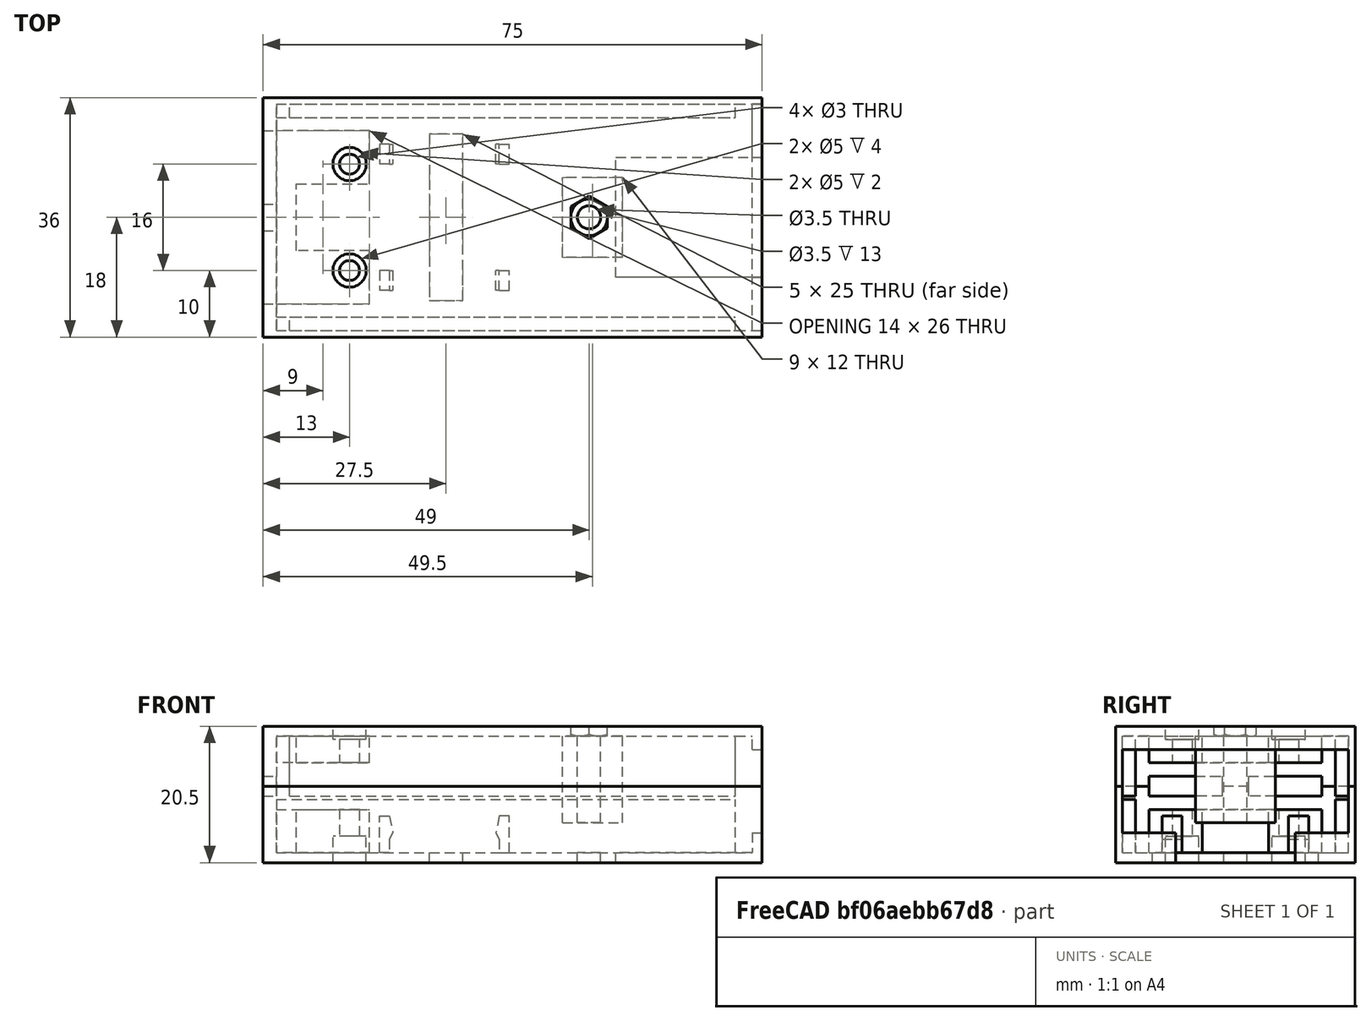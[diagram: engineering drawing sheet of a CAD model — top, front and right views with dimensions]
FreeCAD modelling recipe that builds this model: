
FCSTD DOCUMENT  (FreeCAD 0.17R13522 (Git))
Label: CubeSensor
License: All rights reserved
LicenseURL: http://en.wikipedia.org/wiki/All_rights_reserved
objects: Part::Box×13, Part::Extrusion×9, Sketcher::SketchObject×7, Part::MultiFuse×6, Part::Cylinder×6, Mesh::Feature×3, Part::Cut×2
note: 43 computed .brp shape members not serialized (recipe doc carries the construction recipe); baked Part::Feature solids carry a one-line shape summary decoded from their .brp

FEATURE [Mesh::Feature] dht22
  Placement = pos=(31,0,3) rot=(-0.707107,-0.707107,0;3.14159rad)
FEATURE [Mesh::Feature] gy_30  label="gy-30"
  Placement = pos=(48,16,3) rot=(-0.57735,0.57735,0.57735;4.18879rad)
FEATURE [Mesh::Feature] moisture_sensor
  Placement = pos=(-46,0,10) rot=(0,0,1;0rad)
FEATURE [Sketcher::SketchObject] Sketch
  MapMode = 5
  sketch-geometry (12):
    g0: LineSegment StartX=-25 StartY=18 StartZ=0 EndX=-25 EndY=-18 EndZ=0
    g1: LineSegment StartX=-25 StartY=-18 StartZ=0 EndX=50 EndY=-18 EndZ=0
    g2: LineSegment StartX=50 StartY=-18 StartZ=0 EndX=50 EndY=-9 EndZ=0
    g3: LineSegment StartX=50 StartY=-9 StartZ=0 EndX=28 EndY=-9 EndZ=0
    g4: LineSegment StartX=28 StartY=-9 StartZ=0 EndX=28 EndY=9 EndZ=0
    g5: LineSegment StartX=28 StartY=9 StartZ=0 EndX=50 EndY=9 EndZ=0
    g6: LineSegment StartX=50 StartY=9 StartZ=0 EndX=50 EndY=18 EndZ=0
    g7: LineSegment StartX=50 StartY=18 StartZ=0 EndX=-25 EndY=18 EndZ=0
    g8: LineSegment StartX=3e-12 StartY=-12.5 StartZ=0 EndX=5 EndY=-12.5 EndZ=0
    g9: LineSegment StartX=5 StartY=-12.5 StartZ=0 EndX=5 EndY=12.5 EndZ=0
    g10: LineSegment StartX=5 StartY=12.5 StartZ=0 EndX=-3e-12 EndY=12.5 EndZ=0
    g11: LineSegment StartX=-3e-12 StartY=12.5 StartZ=0 EndX=3e-12 EndY=-12.5 EndZ=0
  constraints (35):
    c: Coincident(g0,g1)
    c: Coincident(g0,g7)
    c: Coincident(g11,g10)
    c: Coincident(g9,g10)
    c: Coincident(g11,g8)
    c: Coincident(g9,g8)
    c: Coincident(g7,g6)
    c: Coincident(g6,g5)
    c: Coincident(g5,g4)
    c: Coincident(g4,g3)
    c: Coincident(g2,g3)
    c: Coincident(g1,g2)
    c: Parallel(g8,g1)
    c: Parallel(g1,g3)
    c: Parallel(g3,g5)
    c: Parallel(g5,g10)
    c: Parallel(g10,g7)
    c: Parallel(g7,g-1)
    c: Parallel(g0,g11)
    c: Parallel(g11,g9)
    c: Parallel(g9,g4)
    c: Parallel(g4,g6)
    c: Parallel(g6,g2)
    c: Equal(g6,g2)
    c: Equal(g5,g3)
    c: DistanceY(g9,g9) = 25
    c: Angle(g1,g0) = 1.5708
    c: DistanceX(g8,g8) = 5
    c: DistanceY(g3,g4) = 18
    c: DistanceY(g5,g6) = 9
    c: DistanceX(g3,g2) = 22
    c: DistanceX(g9,g4) = 23
    c: DistanceX(g0,g10) = 25
    c: Symmetric(g10,g8,g-1)
    c: Symmetric(g3,g4,g-1)
FEATURE [Part::Extrusion] Extrude
  Base = -> Sketch
  Dir = (0,0,1)
  DirMode = 2
  FaceMakerClass = Part::FaceMakerBullseye
  LengthFwd = 1.5
  LengthRev = 0
  Solid = true
  Symmetric = false
FEATURE [Part::Box] Box  label="sidewall1"
  AttacherType = Attacher::AttachEngine3D
  Height = 10
  Length = 75
  Placement = pos=(-25,-18,1.5) rot=(0,0,1;0rad)
  Width = 1
FEATURE [Part::Box] Box001  label="sidewall002"
  AttacherType = Attacher::AttachEngine3D
  Height = 10
  Length = 75
  Placement = pos=(-25,17,1.5) rot=(0,0,1;0rad)
  Width = 1
FEATURE [Part::Box] Box002  label="sidewall003"
  AttacherType = Attacher::AttachEngine3D
  Height = 8
  Length = 71
  Placement = pos=(-25,-17,1.5) rot=(0,0,1;0rad)
  Width = 2
FEATURE [Part::Box] Box003  label="sidewall004"
  AttacherType = Attacher::AttachEngine3D
  Height = 8
  Length = 71
  Placement = pos=(-25,15,1.5) rot=(0,0,1;0rad)
  Width = 2
FEATURE [Part::Box] Box004  label="Cube"
  AttacherType = Attacher::AttachEngine3D
  Height = 3
  Length = 1.5
  Placement = pos=(48.5,9,1.5) rot=(0,0,1;0rad)
  Width = 9
FEATURE [Part::Box] Box005  label="Cube001"
  AttacherType = Attacher::AttachEngine3D
  Height = 3
  Length = 1.5
  Placement = pos=(48.5,-18,1.5) rot=(0,0,1;0rad)
  Width = 9
FEATURE [Sketcher::SketchObject] Sketch001
  MapMode = 5
  Placement = pos=(0,0,0) rot=(0.57735,0.57735,0.57735;2.0944rad)
  sketch-geometry (12):
    g0: LineSegment StartX=-18 StartY=0 StartZ=0 EndX=18 EndY=0 EndZ=0
    g1: LineSegment StartX=18 StartY=0 StartZ=0 EndX=18 EndY=10 EndZ=0
    g2: LineSegment StartX=18 StartY=10 StartZ=0 EndX=13 EndY=10 EndZ=0
    g3: LineSegment StartX=13 StartY=10 StartZ=0 EndX=13 EndY=8.5 EndZ=0
    g4: LineSegment StartX=13 StartY=8.5 StartZ=0 EndX=2 EndY=8.5 EndZ=0
    g5: LineSegment StartX=2 StartY=8.5 StartZ=0 EndX=2 EndY=10 EndZ=0
    g6: LineSegment StartX=2 StartY=10 StartZ=0 EndX=-2 EndY=10 EndZ=0
    g7: LineSegment StartX=-2 StartY=10 StartZ=0 EndX=-2 EndY=8.5 EndZ=0
    g8: LineSegment StartX=-2 StartY=8.5 StartZ=0 EndX=-13 EndY=8.5 EndZ=0
    g9: LineSegment StartX=-13 StartY=8.5 StartZ=0 EndX=-13 EndY=10 EndZ=0
    g10: LineSegment StartX=-13 StartY=10 StartZ=0 EndX=-18 EndY=10 EndZ=0
    g11: LineSegment StartX=-18 StartY=10 StartZ=0 EndX=-18 EndY=0 EndZ=0
  constraints (35):
    c: Coincident(g10,g11)
    c: Coincident(g0,g11)
    c: Coincident(g9,g8)
    c: Coincident(g7,g8)
    c: Coincident(g10,g9)
    c: Coincident(g7,g6)
    c: Coincident(g6,g5)
    c: Coincident(g5,g4)
    c: Coincident(g4,g3)
    c: Coincident(g3,g2)
    c: Coincident(g1,g2)
    c: Coincident(g0,g1)
    c: Parallel(g11,g9)
    c: Parallel(g9,g7)
    c: Parallel(g7,g5)
    c: Parallel(g5,g3)
    c: Parallel(g3,g1)
    c: Parallel(g0,g2)
    c: Parallel(g2,g4)
    c: Parallel(g4,g6)
    c: Parallel(g6,g8)
    c: Parallel(g8,g10)
    c: Angle(g0,g11) = 1.5708
    c: Equal(g10,g2)
    c: Equal(g8,g4)
    c: Equal(g9,g7)
    c: Equal(g7,g5)
    c: Equal(g5,g3)
    c: DistanceY(g8,g9) = 1.5
    c: DistanceX(g4,g3) = 11
    c: DistanceX(g6,g5) = 4
    c: DistanceY(g0,g10) = 10
    c: Symmetric(g0,g0,g-1)
    c: PointOnObject(g0,g-1)
    c: DistanceX(g0,g0) = 36
FEATURE [Part::Extrusion] Extrude001
  Base = -> Sketch001
  Dir = (1,0,0)
  DirMode = 2
  FaceMakerClass = Part::FaceMakerBullseye
  LengthFwd = 2
  LengthRev = 0
  Placement = pos=(-25,0,1.5) rot=(0,0,1;0rad)
  Solid = true
  Symmetric = false
FEATURE [Part::Box] Box007  label="Cube003"
  AttacherType = Attacher::AttachEngine3D
  Height = 1.5
  Length = 75
  Placement = pos=(-25,-18,19) rot=(0,0,1;0rad)
  Width = 36
FEATURE [Part::Box] Box008  label="Cube004"
  AttacherType = Attacher::AttachEngine3D
  Height = 7.5
  Length = 75
  Placement = pos=(-25,-18,11.5) rot=(0,0,1;0rad)
  Width = 1
FEATURE [Part::Box] Box009  label="Cube005"
  AttacherType = Attacher::AttachEngine3D
  Height = 7.5
  Length = 75
  Placement = pos=(-25,17,11.5) rot=(0,0,1;0rad)
  Width = 1
FEATURE [Part::Box] Box010  label="Cube006"
  AttacherType = Attacher::AttachEngine3D
  Height = 9
  Length = 67
  Placement = pos=(-21,-17,10) rot=(0,0,1;0rad)
  Width = 2
FEATURE [Part::Box] Box011  label="Cube007"
  AttacherType = Attacher::AttachEngine3D
  Height = 9
  Length = 67
  Placement = pos=(-21,15,10) rot=(0,0,1;0rad)
  Width = 2
FEATURE [Part::Box] Box012  label="Cube008"
  AttacherType = Attacher::AttachEngine3D
  Height = 2
  Length = 1.5
  Placement = pos=(48.5,-17,17) rot=(0,0,1;0rad)
  Width = 34
FEATURE [Sketcher::SketchObject] Sketch002
  MapMode = 5
  Placement = pos=(0,0,0) rot=(0.57735,0.57735,0.57735;2.0944rad)
  sketch-geometry (12):
    g0: LineSegment StartX=-18 StartY=1e-12 StartZ=0 EndX=-13 EndY=1e-12 EndZ=0
    g1: LineSegment StartX=-13 StartY=1e-12 StartZ=0 EndX=-13 EndY=1.5 EndZ=0
    g2: LineSegment StartX=-13 StartY=1.5 StartZ=0 EndX=-2 EndY=1.5 EndZ=0
    g3: LineSegment StartX=-2 StartY=1.5 StartZ=0 EndX=-2 EndY=1e-12 EndZ=0
    g4: LineSegment StartX=-2 StartY=1e-12 StartZ=0 EndX=2 EndY=1e-12 EndZ=0
    g5: LineSegment StartX=2 StartY=1e-12 StartZ=0 EndX=2 EndY=1.5 EndZ=0
    g6: LineSegment StartX=2 StartY=1.5 StartZ=0 EndX=13 EndY=1.5 EndZ=0
    g7: LineSegment StartX=13 StartY=1.5 StartZ=0 EndX=13 EndY=-1e-12 EndZ=0
    g8: LineSegment StartX=13 StartY=-1e-12 StartZ=0 EndX=18 EndY=-1e-12 EndZ=0
    g9: LineSegment StartX=18 StartY=-1e-12 StartZ=0 EndX=18 EndY=7.5 EndZ=0
    g10: LineSegment StartX=18 StartY=7.5 StartZ=0 EndX=-18 EndY=7.5 EndZ=0
    g11: LineSegment StartX=-18 StartY=7.5 StartZ=0 EndX=-18 EndY=1e-12 EndZ=0
  constraints (36):
    c: Coincident(g2,g3)
    c: Coincident(g4,g3)
    c: Coincident(g6,g5)
    c: Coincident(g5,g4)
    c: Coincident(g1,g2)
    c: Coincident(g0,g1)
    c: Coincident(g7,g6)
    c: Coincident(g7,g8)
    c: Coincident(g8,g9)
    c: Coincident(g10,g9)
    c: Coincident(g0,g11)
    c: Coincident(g10,g11)
    c: Parallel(g0,g10)
    c: Parallel(g10,g2)
    c: Parallel(g2,g4)
    c: Parallel(g4,g6)
    c: Parallel(g6,g8)
    c: Parallel(g11,g1)
    c: Parallel(g1,g3)
    c: Parallel(g3,g5)
    c: Parallel(g5,g7)
    c: Parallel(g7,g9)
    c: Equal(g2,g6)
    c: Equal(g0,g8)
    c: Equal(g11,g9)
    c: Equal(g1,g3)
    c: Equal(g3,g5)
    c: Equal(g5,g7)
    c: DistanceX(g3,g4) = 4
    c: DistanceX(g1,g2) = 11
    c: DistanceY(g0,g10) = 7.5
    c: Angle(g11,g10) = 1.5708
    c: DistanceY(g0,g1) = 1.5
    c: Parallel(g4,g-1)
    c: DistanceX(g10,g9) = 36
    c: Symmetric(g0,g7,g-1)
FEATURE [Part::Extrusion] Extrude002
  Base = -> Sketch002
  Dir = (1,0,0)
  DirMode = 2
  FaceMakerClass = Part::FaceMakerBullseye
  LengthFwd = 2
  LengthRev = 0
  Placement = pos=(-25,0,11.5) rot=(0,0,1;0rad)
  Solid = true
  Symmetric = false
FEATURE [Part::Box] Box015  label="Cube011"
  AttacherType = Attacher::AttachEngine3D
  Height = 14.5
  Length = 9
  Placement = pos=(20,-6,6) rot=(0,0,1;0rad)
  Width = 12
FEATURE [Sketcher::SketchObject] Sketch003
  MapMode = 5
  sketch-geometry (10):
    g0: LineSegment StartX=-3 StartY=13 StartZ=0 EndX=11 EndY=13 EndZ=0
    g1: LineSegment StartX=11 StartY=-13 StartZ=0 EndX=-3 EndY=-13 EndZ=0
    g2: LineSegment StartX=-3 StartY=-13 StartZ=0 EndX=-3 EndY=13 EndZ=0
    g3: LineSegment StartX=11 StartY=13 StartZ=0 EndX=11 EndY=5 EndZ=0
    g4: LineSegment StartX=11 StartY=5 StartZ=0 EndX=0 EndY=5 EndZ=0
    g5: LineSegment StartX=0 StartY=5 StartZ=0 EndX=0 EndY=-5 EndZ=0
    g6: LineSegment StartX=0 StartY=-5 StartZ=0 EndX=11 EndY=-5 EndZ=0
    g7: LineSegment StartX=11 StartY=-5 StartZ=0 EndX=11 EndY=-13 EndZ=0
    g8: Circle CenterX=8 CenterY=8 CenterZ=0 NormalX=0 NormalY=0 NormalZ=1 AngleXU=0 Radius=1.5
    g9: Circle CenterX=8 CenterY=-8 CenterZ=0 NormalX=0 NormalY=0 NormalZ=1 AngleXU=0 Radius=1.5
  constraints (30):
    c: Coincident(g2,g0)
    c: Coincident(g3,g0)
    c: Coincident(g4,g3)
    c: Coincident(g5,g4)
    c: Coincident(g5,g6)
    c: Coincident(g7,g6)
    c: Coincident(g7,g1)
    c: Coincident(g1,g2)
    c: Parallel(g7,g2)
    c: Parallel(g2,g5)
    c: Parallel(g5,g3)
    c: Parallel(g4,g6)
    c: Parallel(g6,g0)
    c: Parallel(g0,g1)
    c: Angle(g1,g2) = 1.5708
    c: Equal(g3,g7)
    c: Equal(g0,g1)
    c: Equal(g4,g6)
    c: Radius(g8) = 1.5
    c: Radius(g9) = 1.5
    c: DistanceX(g0,g4) = 3
    c: Parallel(g-1,g6)
    c: DistanceX(g4,g3) = 11
    c: DistanceY(g5,g4) = 10
    c: DistanceY(g1,g0) = 26
    c: DistanceY(g9,g8) = 16
    c: DistanceX(g9,g6) = 3
    c: DistanceX(g8,g3) = 3
    c: DistanceY(g3,g8) = 3
    c: Symmetric(g4,g5,g-1)
FEATURE [Sketcher::SketchObject] Sketch004
  MapMode = 5
  sketch-geometry (10):
    g0: LineSegment StartX=-3 StartY=13 StartZ=0 EndX=11 EndY=13 EndZ=0
    g1: LineSegment StartX=11 StartY=-13 StartZ=0 EndX=-3 EndY=-13 EndZ=0
    g2: LineSegment StartX=-3 StartY=-13 StartZ=0 EndX=-3 EndY=13 EndZ=0
    g3: LineSegment StartX=11 StartY=13 StartZ=0 EndX=11 EndY=5 EndZ=0
    g4: LineSegment StartX=11 StartY=5 StartZ=0 EndX=0 EndY=5 EndZ=0
    g5: LineSegment StartX=0 StartY=5 StartZ=0 EndX=0 EndY=-5 EndZ=0
    g6: LineSegment StartX=0 StartY=-5 StartZ=0 EndX=11 EndY=-5 EndZ=0
    g7: LineSegment StartX=11 StartY=-5 StartZ=0 EndX=11 EndY=-13 EndZ=0
    g8: Circle CenterX=8 CenterY=8 CenterZ=0 NormalX=0 NormalY=0 NormalZ=1 AngleXU=0 Radius=1.5
    g9: Circle CenterX=8 CenterY=-8 CenterZ=0 NormalX=0 NormalY=0 NormalZ=1 AngleXU=0 Radius=1.5
  constraints (30):
    c: Coincident(g2,g0)
    c: Coincident(g3,g0)
    c: Coincident(g4,g3)
    c: Coincident(g5,g4)
    c: Coincident(g5,g6)
    c: Coincident(g7,g6)
    c: Coincident(g7,g1)
    c: Coincident(g1,g2)
    c: Parallel(g7,g2)
    c: Parallel(g2,g5)
    c: Parallel(g5,g3)
    c: Parallel(g4,g6)
    c: Parallel(g6,g0)
    c: Parallel(g0,g1)
    c: Angle(g1,g2) = 1.5708
    c: Equal(g3,g7)
    c: Equal(g0,g1)
    c: Equal(g4,g6)
    c: Radius(g8) = 1.5
    c: Radius(g9) = 1.5
    c: DistanceX(g0,g4) = 3
    c: Parallel(g-1,g6)
    c: DistanceX(g4,g3) = 11
    c: DistanceY(g5,g4) = 10
    c: DistanceY(g1,g0) = 26
    c: DistanceY(g9,g8) = 16
    c: DistanceX(g9,g6) = 3
    c: DistanceX(g8,g3) = 3
    c: DistanceY(g3,g8) = 3
    c: Symmetric(g4,g5,g-1)
FEATURE [Part::Extrusion] Extrude003
  Base = -> Sketch004
  Dir = (0,0,1)
  DirMode = 2
  FaceMakerClass = Part::FaceMakerBullseye
  LengthFwd = 8
  LengthRev = 0
  Placement = pos=(-20,0,0) rot=(0,0,1;0rad)
  Solid = true
  Symmetric = false
FEATURE [Part::Extrusion] Extrude004
  Base = -> Sketch003
  Dir = (0,0,1)
  DirMode = 2
  FaceMakerClass = Part::FaceMakerBullseye
  LengthFwd = 5.5
  LengthRev = 0
  Placement = pos=(-20,0,15) rot=(0,0,1;0rad)
  Solid = true
  Symmetric = false
FEATURE [Part::MultiFuse] Fusion001  label="OutercaseSide2"
  Shapes = -> [Box007,Box012,Box010,Box009,Box008,Extrude002,Box015,Box011,Extrude004]
FEATURE [Part::Cylinder] Cylinder001
  Angle = 360
  AttacherType = Attacher::AttachEngine3D
  Height = 19
  Placement = pos=(24,0,4) rot=(0,0,1;0rad)
  Radius = 1.75
FEATURE [Part::MultiFuse] Fusion004  label="M3_003"
  Placement = pos=(24,0,19) rot=(0,0,1;0rad)
FEATURE [Part::Cylinder] Cylinder002
  Angle = 360
  AttacherType = Attacher::AttachEngine3D
  Height = 19
  Placement = pos=(24,0,-8) rot=(0,0,1;0rad)
  Radius = 1.75
FEATURE [Part::Cylinder] Cylinder003
  Angle = 360
  AttacherType = Attacher::AttachEngine3D
  Height = 4
  Placement = pos=(-12,-8,0) rot=(0,0,1;0rad)
  Radius = 2.5
FEATURE [Part::Cylinder] Cylinder004
  Angle = 360
  AttacherType = Attacher::AttachEngine3D
  Height = 4
  Placement = pos=(-12,8,0) rot=(0,0,1;0rad)
  Radius = 2.5
FEATURE [Part::MultiFuse] Fusion005  label="HolesSide1"
  Shapes = -> [Cylinder004,Cylinder002,Cylinder003]
FEATURE [Part::Cylinder] Cylinder005
  Angle = 360
  AttacherType = Attacher::AttachEngine3D
  Height = 2
  Placement = pos=(-12,-8,18.5) rot=(0,0,1;0rad)
  Radius = 2.5
FEATURE [Part::Cylinder] Cylinder006
  Angle = 360
  AttacherType = Attacher::AttachEngine3D
  Height = 2
  Placement = pos=(-12,8,18.5) rot=(0,0,1;0rad)
  Radius = 2.5
FEATURE [Part::MultiFuse] Fusion006  label="HolesSide2"
  Shapes = -> [Fusion004,Cylinder006,Cylinder005,Cylinder001]
FEATURE [Part::Cut] Cut  label="Side2withHoles"
  Base = -> Fusion001
  Tool = -> Fusion006
FEATURE [Sketcher::SketchObject] Sketch006
  MapMode = 5
  Placement = pos=(0,0,0) rot=(1,0,0;1.5708rad)
  sketch-geometry (6):
    g0: LineSegment StartX=0 StartY=0 StartZ=0 EndX=-1.5 EndY=0 EndZ=0
    g1: LineSegment StartX=-1.5 StartY=0 StartZ=0 EndX=-1.5 EndY=5.5 EndZ=0
    g2: LineSegment StartX=-1.5 StartY=5.5 StartZ=0 EndX=0 EndY=5.5 EndZ=0
    g3: LineSegment StartX=0 StartY=5.5 StartZ=0 EndX=0.5 EndY=3 EndZ=0
    g4: LineSegment StartX=0.5 StartY=3 StartZ=0 EndX=0 EndY=2 EndZ=0
    g5: LineSegment StartX=0 StartY=2 StartZ=0 EndX=0 EndY=0 EndZ=0
  constraints (17):
    c: Coincident(g5,g0)
    c: Coincident(g4,g5)
    c: Coincident(g4,g3)
    c: Coincident(g2,g3)
    c: Coincident(g1,g2)
    c: Coincident(g1,g0)
    c: Parallel(g0,g2)
    c: Parallel(g2,g-1)
    c: Parallel(g1,g5)
    c: Parallel(g5,g-2)
    c: Equal(g2,g0)
    c: DistanceX(g0,g0) = 1.5
    c: Coincident(g0,g-1)
    c: DistanceY(g-1,g4) = 2
    c: DistanceY(g0,g1) = 5.5
    c: DistanceX(g4,g3) = 0.5
    c: DistanceY(g4,g3) = 1
FEATURE [Part::Extrusion] Extrude005
  Base = -> Sketch006
  Dir = (0,-1,0)
  DirMode = 2
  FaceMakerClass = Part::FaceMakerBullseye
  LengthFwd = 3
  LengthRev = 0
  Placement = pos=(-6,11,1.5) rot=(0,0,1;0rad)
  Solid = true
  Symmetric = false
FEATURE [Part::Extrusion] Extrude006
  Base = -> Sketch006
  Dir = (0,-1,0)
  DirMode = 2
  FaceMakerClass = Part::FaceMakerBullseye
  LengthFwd = 3
  LengthRev = 0
  Placement = pos=(-6,-8,1.5) rot=(0,0,1;0rad)
  Solid = true
  Symmetric = false
FEATURE [Part::Extrusion] Extrude007
  Base = -> Sketch006
  Dir = (0,-1,0)
  DirMode = 2
  FaceMakerClass = Part::FaceMakerBullseye
  LengthFwd = 3
  LengthRev = 0
  Placement = pos=(10.5,8,1.5) rot=(0,0,1;3.14159rad)
  Solid = true
  Symmetric = false
FEATURE [Sketcher::SketchObject] Sketch007
  MapMode = 5
  Placement = pos=(0,0,0) rot=(1,0,0;1.5708rad)
  sketch-geometry (6):
    g0: LineSegment StartX=0 StartY=0 StartZ=0 EndX=-1.5 EndY=0 EndZ=0
    g1: LineSegment StartX=-1.5 StartY=0 StartZ=0 EndX=-1.5 EndY=5.5 EndZ=0
    g2: LineSegment StartX=-1.5 StartY=5.5 StartZ=0 EndX=0 EndY=5.5 EndZ=0
    g3: LineSegment StartX=0 StartY=5.5 StartZ=0 EndX=0.5 EndY=3 EndZ=0
    g4: LineSegment StartX=0.5 StartY=3 StartZ=0 EndX=0 EndY=2 EndZ=0
    g5: LineSegment StartX=0 StartY=2 StartZ=0 EndX=0 EndY=0 EndZ=0
  constraints (17):
    c: Coincident(g5,g0)
    c: Coincident(g4,g5)
    c: Coincident(g4,g3)
    c: Coincident(g2,g3)
    c: Coincident(g1,g2)
    c: Coincident(g1,g0)
    c: Parallel(g0,g2)
    c: Parallel(g2,g-1)
    c: Parallel(g1,g5)
    c: Parallel(g5,g-2)
    c: Equal(g2,g0)
    c: DistanceX(g0,g0) = 1.5
    c: Coincident(g0,g-1)
    c: DistanceY(g-1,g4) = 2
    c: DistanceY(g0,g1) = 5.5
    c: DistanceX(g4,g3) = 0.5
    c: DistanceY(g4,g3) = 1
FEATURE [Part::Extrusion] Extrude008
  Base = -> Sketch007
  Dir = (0,-1,0)
  DirMode = 2
  FaceMakerClass = Part::FaceMakerBullseye
  LengthFwd = 3
  LengthRev = 0
  Placement = pos=(10.5,-11,1.5) rot=(0,0,1;3.14159rad)
  Solid = true
  Symmetric = false
FEATURE [Part::MultiFuse] Fusion007  label="pcb_holder"
  Shapes = -> [Extrude005,Extrude008,Extrude007,Extrude006]
FEATURE [Part::MultiFuse] Fusion  label="OutercaseSide1"
  Shapes = -> [Box,Box003,Box004,Box005,Box001,Box002,Extrude001,Extrude,Extrude003,Fusion007]
FEATURE [Part::Cut] Cut001  label="Side1WithHoles"
  Base = -> Fusion
  Tool = -> Fusion005
